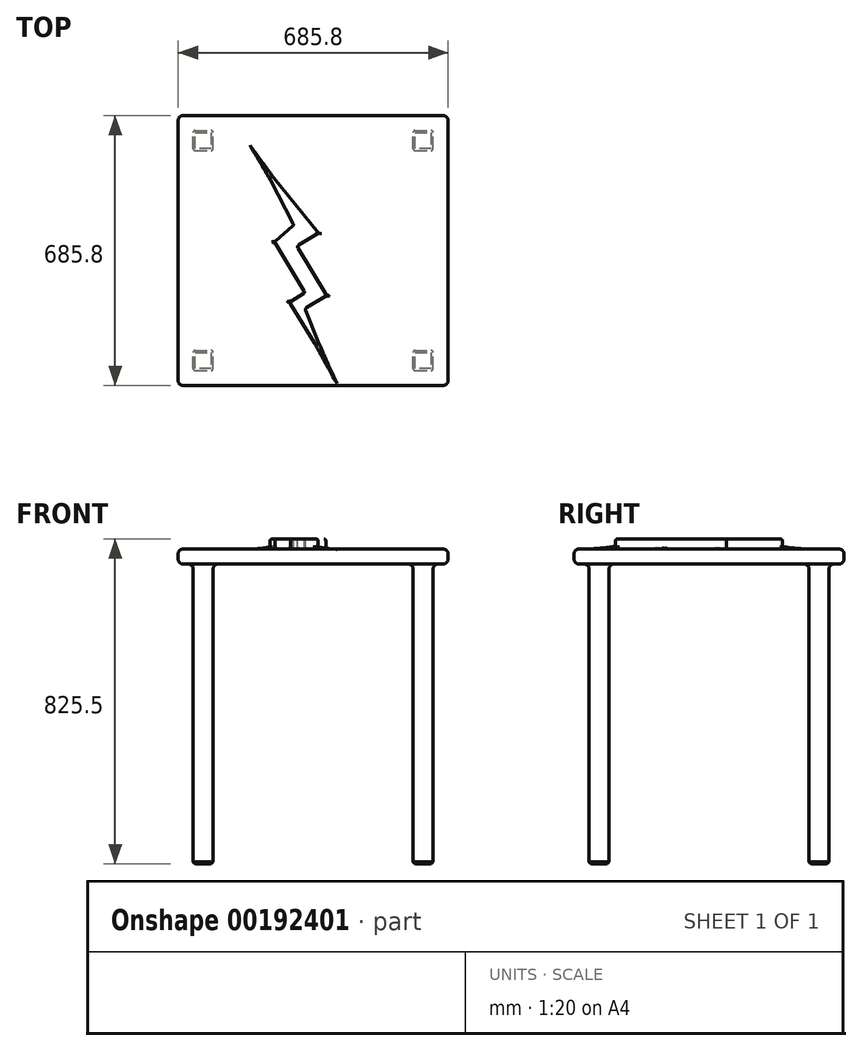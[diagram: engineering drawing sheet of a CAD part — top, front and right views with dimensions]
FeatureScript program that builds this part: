
annotation { "Feature Type Name" : "Feature", "Feature Type Description" : "" }
export const myFeature = defineFeature(function(context is Context, id is Id, definition is map)
    precondition{}
    {
        {
            var Q0;
            Q0=qCreatedBy(makeId("Top.planeOp"),FACE);
            cPlane(context, id + "F0", {"entities" : qUnion([Q0]), "cplaneType" : CPlaneType.OFFSET, "offset" : 457.2 * mm, "width" : 152.4 * mm, "height" : 152.4 * mm});
        }
        {
            var Q0;
            Q0=qCreatedBy(id+"F0.planeOp",FACE);
            var sketch = newSketch(context, id + "F1", { "sketchPlane" : qUnion([Q0])});
            skLineSegment(sketch, "E0.bottom", {"start": v(-322.49, 342.9) * mm, "end": v(363.31, 342.9) * mm});
            skLineSegment(sketch, "E0.top", {"start": v(-322.49, -342.9) * mm, "end": v(363.31, -342.9) * mm});
            skLineSegment(sketch, "E0.left", {"start": v(-322.49, 342.9) * mm, "end": v(-322.49, -342.9) * mm});
            skLineSegment(sketch, "E0.right", {"start": v(363.31, 342.9) * mm, "end": v(363.31, -342.9) * mm});
            skPoint(sketch, "E0.middle", {"position": v(20.41, 0) * mm});
            skSolve(sketch);
        }
        {
            var Q0;
            Q0=makeQuery(id+"F1.imprint","IMPRINT",FACE,{"disambiguationData":[TD([[makeQuery(id+"F1.imprint","IMPRINT",EDGE,{"derivedFrom":sQuery(id+"F1.wireOp",EDGE,"E0.bottom")}),-1.0]])]});
            extrude(context, id + "F2", {"entities" : qUnion([Q0]), "depth" : 38.1 * mm});
        }
        {
            var Q0;
            Q0=makeQuery(id+"F2.opExtrude","CAP_FACE",FACE,{"disambiguationData":[OSD([sQuery(id+"F1.wireOp",EDGE,"E0.bottom"),sQuery(id+"F1.wireOp",EDGE,"E0.top"),sQuery(id+"F1.wireOp",EDGE,"E0.left"),sQuery(id+"F1.wireOp",EDGE,"E0.right")])],"isStart":true});
            var sketch = newSketch(context, id + "F3", { "sketchPlane" : qUnion([Q0])});
            skLineSegment(sketch, "E1.bottom", {"start": v(-284.39, 304.8) * mm, "end": v(-233.59, 304.8) * mm});
            skLineSegment(sketch, "E1.top", {"start": v(-284.39, 254) * mm, "end": v(-233.59, 254) * mm});
            skLineSegment(sketch, "E1.left", {"start": v(-284.39, 304.8) * mm, "end": v(-284.39, 254) * mm});
            skLineSegment(sketch, "E1.right", {"start": v(-233.59, 304.8) * mm, "end": v(-233.59, 254) * mm});
            skPoint(sketch, "E1.middle", {"position": v(-258.99, 279.4) * mm});
            skLineSegment(sketch, "E2.bottom", {"start": v(274.41, 304.8) * mm, "end": v(325.21, 304.8) * mm});
            skLineSegment(sketch, "E2.top", {"start": v(274.41, 254) * mm, "end": v(325.21, 254) * mm});
            skLineSegment(sketch, "E2.left", {"start": v(274.41, 304.8) * mm, "end": v(274.41, 254) * mm});
            skLineSegment(sketch, "E2.right", {"start": v(325.21, 304.8) * mm, "end": v(325.21, 254) * mm});
            skPoint(sketch, "E2.middle", {"position": v(299.81, 279.4) * mm});
            skPoint(sketch, "E3.MirrorP", {"position": v(202.34, 274.07) * mm});
            skLineSegment(sketch, "E4.bottom", {"start": v(274.41, -254) * mm, "end": v(325.21, -254) * mm});
            skLineSegment(sketch, "E4.top", {"start": v(274.41, -304.8) * mm, "end": v(325.21, -304.8) * mm});
            skLineSegment(sketch, "E4.left", {"start": v(274.41, -254) * mm, "end": v(274.41, -304.8) * mm});
            skLineSegment(sketch, "E4.right", {"start": v(325.21, -254) * mm, "end": v(325.21, -304.8) * mm});
            skPoint(sketch, "E4.middle", {"position": v(299.81, -279.4) * mm});
            skLineSegment(sketch, "E5.bottom", {"start": v(-284.39, -254) * mm, "end": v(-233.59, -254) * mm});
            skLineSegment(sketch, "E5.top", {"start": v(-284.39, -304.8) * mm, "end": v(-233.59, -304.8) * mm});
            skLineSegment(sketch, "E5.left", {"start": v(-284.39, -254) * mm, "end": v(-284.39, -304.8) * mm});
            skLineSegment(sketch, "E5.right", {"start": v(-233.59, -254) * mm, "end": v(-233.59, -304.8) * mm});
            skPoint(sketch, "E5.middle", {"position": v(-258.99, -279.4) * mm});
            skSolve(sketch);
        }
        {
            var Q0;
            Q0=makeQuery(id+"F3.imprint","IMPRINT",FACE,{"disambiguationData":[TD([[makeQuery(id+"F3.imprint","IMPRINT",EDGE,{"derivedFrom":sQuery(id+"F3.wireOp",EDGE,"E1.bottom")}),-1.0]])]});
            var Q1;
            Q1=makeQuery(id+"F3.imprint","IMPRINT",FACE,{"disambiguationData":[TD([[makeQuery(id+"F3.imprint","IMPRINT",EDGE,{"derivedFrom":sQuery(id+"F3.wireOp",EDGE,"E5.bottom")}),-1.0]])]});
            var Q2;
            Q2=makeQuery(id+"F3.imprint","IMPRINT",FACE,{"disambiguationData":[TD([[makeQuery(id+"F3.imprint","IMPRINT",EDGE,{"derivedFrom":sQuery(id+"F3.wireOp",EDGE,"E4.bottom")}),-1.0]])]});
            var Q3;
            Q3=makeQuery(id+"F3.imprint","IMPRINT",FACE,{"disambiguationData":[TD([[makeQuery(id+"F3.imprint","IMPRINT",EDGE,{"derivedFrom":sQuery(id+"F3.wireOp",EDGE,"E2.bottom")}),-1.0]])]});
            extrude(context, id + "F4", {"entities" : qUnion([Q0, Q1, Q2, Q3]), "operationType" : NewBodyOperationType.ADD, "depth" : 762 * mm});
        }
        {
            var Q0;
            Q0=makeQuery(id+"F4.opExtrude","SWEPT_EDGE",EDGE,{"disambiguationData":[OSD([sQuery(id+"F3.wireOp",EDGE,"E1.bottom"),sQuery(id+"F3.wireOp",EDGE,"E1.right")])]});
            var Q1;
            Q1=makeQuery(id+"F4.opExtrude","SWEPT_EDGE",EDGE,{"disambiguationData":[OSD([sQuery(id+"F3.wireOp",EDGE,"E1.bottom"),sQuery(id+"F3.wireOp",EDGE,"E1.left")])]});
            var Q2;
            Q2=makeQuery(id+"F4.opExtrude","SWEPT_EDGE",EDGE,{"disambiguationData":[OSD([sQuery(id+"F3.wireOp",EDGE,"E1.top"),sQuery(id+"F3.wireOp",EDGE,"E1.right")])]});
            var Q3;
            Q3=makeQuery(id+"F4.opExtrude","SWEPT_EDGE",EDGE,{"disambiguationData":[OSD([sQuery(id+"F3.wireOp",EDGE,"E1.top"),sQuery(id+"F3.wireOp",EDGE,"E1.left")])]});
            var Q4;
            Q4=makeQuery(id+"F4.opExtrude","SWEPT_EDGE",EDGE,{"disambiguationData":[OSD([sQuery(id+"F3.wireOp",EDGE,"E5.top"),sQuery(id+"F3.wireOp",EDGE,"E5.left")])]});
            var Q5;
            Q5=makeQuery(id+"F4.opExtrude","SWEPT_EDGE",EDGE,{"disambiguationData":[OSD([sQuery(id+"F3.wireOp",EDGE,"E5.top"),sQuery(id+"F3.wireOp",EDGE,"E5.right")])]});
            var Q6;
            Q6=makeQuery(id+"F4.opExtrude","SWEPT_EDGE",EDGE,{"disambiguationData":[OSD([sQuery(id+"F3.wireOp",EDGE,"E5.bottom"),sQuery(id+"F3.wireOp",EDGE,"E5.left")])]});
            var Q7;
            Q7=makeQuery(id+"F4.opExtrude","SWEPT_EDGE",EDGE,{"disambiguationData":[OSD([sQuery(id+"F3.wireOp",EDGE,"E5.bottom"),sQuery(id+"F3.wireOp",EDGE,"E5.right")])]});
            var Q8;
            Q8=makeQuery(id+"F4.opExtrude","SWEPT_EDGE",EDGE,{"disambiguationData":[OSD([sQuery(id+"F3.wireOp",EDGE,"E4.top"),sQuery(id+"F3.wireOp",EDGE,"E4.left")])]});
            var Q9;
            Q9=makeQuery(id+"F4.opExtrude","SWEPT_EDGE",EDGE,{"disambiguationData":[OSD([sQuery(id+"F3.wireOp",EDGE,"E4.top"),sQuery(id+"F3.wireOp",EDGE,"E4.right")])]});
            var Q10;
            Q10=makeQuery(id+"F4.opExtrude","SWEPT_EDGE",EDGE,{"disambiguationData":[OSD([sQuery(id+"F3.wireOp",EDGE,"E4.bottom"),sQuery(id+"F3.wireOp",EDGE,"E4.right")])]});
            var Q11;
            Q11=makeQuery(id+"F4.opExtrude","SWEPT_EDGE",EDGE,{"disambiguationData":[OSD([sQuery(id+"F3.wireOp",EDGE,"E2.top"),sQuery(id+"F3.wireOp",EDGE,"E2.right")])]});
            var Q12;
            Q12=makeQuery(id+"F4.opExtrude","SWEPT_EDGE",EDGE,{"disambiguationData":[OSD([sQuery(id+"F3.wireOp",EDGE,"E2.top"),sQuery(id+"F3.wireOp",EDGE,"E2.left")])]});
            var Q13;
            Q13=makeQuery(id+"F4.opExtrude","SWEPT_EDGE",EDGE,{"disambiguationData":[OSD([sQuery(id+"F3.wireOp",EDGE,"E2.bottom"),sQuery(id+"F3.wireOp",EDGE,"E2.right")])]});
            var Q14;
            Q14=makeQuery(id+"F4.opExtrude","SWEPT_EDGE",EDGE,{"disambiguationData":[OSD([sQuery(id+"F3.wireOp",EDGE,"E2.bottom"),sQuery(id+"F3.wireOp",EDGE,"E2.left")])]});
            var Q15;
            Q15=makeQuery(id+"F4.opExtrude","SWEPT_EDGE",EDGE,{"disambiguationData":[OSD([sQuery(id+"F3.wireOp",EDGE,"E4.bottom"),sQuery(id+"F3.wireOp",EDGE,"E4.left")])]});
            fillet(context, id + "F5", {"entities" : qUnion([Q0, Q1, Q2, Q3, Q4, Q5, Q6, Q7, Q8, Q9, Q10, Q11, Q12, Q13, Q14, Q15]), "radius" : 5.08 * mm, "tangentPropagation" : true, "allowEdgeOverflow" : false});
        }
        {
            var Q0;
            Q0=makeQuery(id+"F4.opExtrude","CAP_FACE",FACE,{"disambiguationData":[OSD([sQuery(id+"F3.wireOp",EDGE,"E2.bottom"),sQuery(id+"F3.wireOp",EDGE,"E2.top"),sQuery(id+"F3.wireOp",EDGE,"E2.left"),sQuery(id+"F3.wireOp",EDGE,"E2.right")])],"isStart":false});
            var Q1;
            Q1=makeQuery(id+"F4.opExtrude","CAP_FACE",FACE,{"disambiguationData":[OSD([sQuery(id+"F3.wireOp",EDGE,"E1.bottom"),sQuery(id+"F3.wireOp",EDGE,"E1.top"),sQuery(id+"F3.wireOp",EDGE,"E1.left"),sQuery(id+"F3.wireOp",EDGE,"E1.right")])],"isStart":false});
            var Q2;
            Q2=makeQuery(id+"F4.opExtrude","CAP_FACE",FACE,{"disambiguationData":[OSD([sQuery(id+"F3.wireOp",EDGE,"E4.bottom"),sQuery(id+"F3.wireOp",EDGE,"E4.top"),sQuery(id+"F3.wireOp",EDGE,"E4.left"),sQuery(id+"F3.wireOp",EDGE,"E4.right")])],"isStart":false});
            chamfer(context, id + "F6", {"entities" : qUnion([Q0, Q1, Q2]), "width" : 5.08 * mm, "tangentPropagation" : true});
        }
        {
            var Q0;
            Q0=makeQuery(id+"F4.opExtrude","CAP_FACE",FACE,{"disambiguationData":[OSD([sQuery(id+"F3.wireOp",EDGE,"E5.bottom"),sQuery(id+"F3.wireOp",EDGE,"E5.top"),sQuery(id+"F3.wireOp",EDGE,"E5.left"),sQuery(id+"F3.wireOp",EDGE,"E5.right")])],"isStart":false});
            chamfer(context, id + "F7", {"entities" : qUnion([Q0]), "width" : 5.08 * mm, "tangentPropagation" : true});
        }
        {
            var Q0;
            Q0=makeQuery(id+"F2.opExtrude","SWEPT_FACE",FACE,{"disambiguationData":[OSD([sQuery(id+"F1.wireOp",EDGE,"E0.top")])]});
            var Q1;
            Q1=makeQuery(id+"F2.opExtrude","SWEPT_FACE",FACE,{"disambiguationData":[OSD([sQuery(id+"F1.wireOp",EDGE,"E0.left")])]});
            var Q2;
            Q2=makeQuery(id+"F2.opExtrude","SWEPT_FACE",FACE,{"disambiguationData":[OSD([sQuery(id+"F1.wireOp",EDGE,"E0.bottom")])]});
            var Q3;
            Q3=makeQuery(id+"F2.opExtrude","SWEPT_FACE",FACE,{"disambiguationData":[OSD([sQuery(id+"F1.wireOp",EDGE,"E0.right")])]});
            var Q4;
            Q4=makeQuery(id+"F2.opExtrude","CAP_FACE",FACE,{"disambiguationData":[OSD([sQuery(id+"F1.wireOp",EDGE,"E0.bottom"),sQuery(id+"F1.wireOp",EDGE,"E0.top"),sQuery(id+"F1.wireOp",EDGE,"E0.left"),sQuery(id+"F1.wireOp",EDGE,"E0.right")])],"isStart":false});
            var Q5;
            Q5=makeQuery(id+"F2.opExtrude","CAP_FACE",FACE,{"disambiguationData":[OSD([sQuery(id+"F1.wireOp",EDGE,"E0.bottom"),sQuery(id+"F1.wireOp",EDGE,"E0.top"),sQuery(id+"F1.wireOp",EDGE,"E0.left"),sQuery(id+"F1.wireOp",EDGE,"E0.right")])],"isStart":true});
            fillet(context, id + "F8", {"entities" : qUnion([Q0, Q1, Q2, Q3, Q4, Q5]), "radius" : 12.7 * mm, "tangentPropagation" : true, "allowEdgeOverflow" : false});
        }
        {
            var Q0;
            Q0=makeQuery(id+"F2.opExtrude","CAP_FACE",FACE,{"disambiguationData":[OSD([sQuery(id+"F1.wireOp",EDGE,"E0.bottom"),sQuery(id+"F1.wireOp",EDGE,"E0.top"),sQuery(id+"F1.wireOp",EDGE,"E0.left"),sQuery(id+"F1.wireOp",EDGE,"E0.right")])],"isStart":false});
            var sketch = newSketch(context, id + "F9", { "sketchPlane" : qUnion([Q0])});
            skLineSegment(sketch, "E6", {"start": v(-112.18, 224.79) * mm, "end": v(-28.45, 64.86) * mm});
            skLineSegment(sketch, "E7", {"start": v(-28.45, 64.86) * mm, "end": v(-77.77, 21.02) * mm});
            skLineSegment(sketch, "E8", {"start": v(-77.77, 21.02) * mm, "end": v(0, -107.1) * mm});
            skLineSegment(sketch, "E9", {"start": v(0, -107.1) * mm, "end": v(-39.5, -131.08) * mm});
            skLineSegment(sketch, "E10", {"start": v(-39.5, -131.08) * mm, "end": v(54.73, -286.32) * mm});
            skLineSegment(sketch, "E11", {"start": v(54.73, -286.32) * mm, "end": v(0, -147.18) * mm});
            skLineSegment(sketch, "E12", {"start": v(0, -147.18) * mm, "end": v(54.73, -113.95) * mm});
            skLineSegment(sketch, "E13", {"start": v(54.73, -113.95) * mm, "end": v(-21.01, 10.82) * mm});
            skLineSegment(sketch, "E14", {"start": v(-21.01, 10.82) * mm, "end": v(33.95, 44.19) * mm});
            skLineSegment(sketch, "E15", {"start": v(33.95, 44.19) * mm, "end": v(-112.18, 224.79) * mm});
            skSolve(sketch);
        }
        {
            var Q0;
            Q0=makeQuery(id+"F9.imprint","IMPRINT",FACE,{"disambiguationData":[TD([[makeQuery(id+"F9.imprint","IMPRINT",EDGE,{"derivedFrom":sQuery(id+"F9.wireOp",EDGE,"E6")}),1.0]])]});
            extrude(context, id + "F10", {"entities" : qUnion([Q0]), "operationType" : NewBodyOperationType.ADD, "depth" : 25.4 * mm});
        }
        {
            var Q0;
            Q0=makeQuery(id+"F2.opExtrude","CAP_FACE",FACE,{"disambiguationData":[OSD([sQuery(id+"F1.wireOp",EDGE,"E0.bottom"),sQuery(id+"F1.wireOp",EDGE,"E0.top"),sQuery(id+"F1.wireOp",EDGE,"E0.left"),sQuery(id+"F1.wireOp",EDGE,"E0.right")])],"isStart":false});
            fillet(context, id + "F11", {"entities" : qUnion([Q0]), "radius" : 5.08 * mm, "tangentPropagation" : true, "allowEdgeOverflow" : false});
        }
        {
            var Q0;
            Q0=makeQuery(id+"F10.opExtrude","CAP_EDGE",EDGE,{"disambiguationData":[OSD([sQuery(id+"F9.wireOp",EDGE,"E7")])],"isStart":false});
            var Q1;
            Q1=makeQuery(id+"F10.opExtrude","CAP_EDGE",EDGE,{"disambiguationData":[OSD([sQuery(id+"F9.wireOp",EDGE,"E8")])],"isStart":false});
            var Q2;
            {var subQ0=sQuery(id+"F9.wireOp",EDGE,"E11");Q2=makeQuery(id+"F11.opFillet","BLEND_EDGE",EDGE,{"blendedFrom":[makeQuery(id+"F10.opExtrude","CAP_EDGE",EDGE,{"disambiguationData":[OSD([subQ0])],"isStart":true}),makeQuery(id+"F10.opExtrude","SWEPT_FACE",FACE,{"disambiguationData":[OSD([subQ0])]})],"blendedInto":[makeQuery(id+"F10.opExtrude","SWEPT_FACE",FACE,{"disambiguationData":[OSD([subQ0])]})]});}
            var Q3;
            {var subQ0=sQuery(id+"F9.wireOp",EDGE,"E10");Q3=makeQuery(id+"F11.opFillet","BLEND_EDGE",EDGE,{"blendedFrom":[makeQuery(id+"F10.opExtrude","CAP_EDGE",EDGE,{"disambiguationData":[OSD([subQ0])],"isStart":true}),makeQuery(id+"F10.opExtrude","SWEPT_FACE",FACE,{"disambiguationData":[OSD([subQ0])]})],"blendedInto":[makeQuery(id+"F10.opExtrude","SWEPT_FACE",FACE,{"disambiguationData":[OSD([subQ0])]})]});}
            var Q4;
            Q4=makeQuery(id+"F10.opExtrude","CAP_EDGE",EDGE,{"disambiguationData":[OSD([sQuery(id+"F9.wireOp",EDGE,"E6")])],"isStart":false});
            var Q5;
            Q5=makeQuery(id+"F10.opExtrude","CAP_EDGE",EDGE,{"disambiguationData":[OSD([sQuery(id+"F9.wireOp",EDGE,"E9")])],"isStart":false});
            var Q6;
            Q6=makeQuery(id+"F10.opExtrude","CAP_EDGE",EDGE,{"disambiguationData":[OSD([sQuery(id+"F9.wireOp",EDGE,"E10")])],"isStart":false});
            var Q7;
            Q7=makeQuery(id+"F10.opExtrude","CAP_EDGE",EDGE,{"disambiguationData":[OSD([sQuery(id+"F9.wireOp",EDGE,"E11")])],"isStart":false});
            var Q8;
            Q8=makeQuery(id+"F10.opExtrude","CAP_EDGE",EDGE,{"disambiguationData":[OSD([sQuery(id+"F9.wireOp",EDGE,"E12")])],"isStart":false});
            var Q9;
            Q9=makeQuery(id+"F10.opExtrude","CAP_EDGE",EDGE,{"disambiguationData":[OSD([sQuery(id+"F9.wireOp",EDGE,"E13")])],"isStart":false});
            var Q10;
            {var subQ0=sQuery(id+"F9.wireOp",EDGE,"E14");Q10=makeQuery(id+"F11.opFillet","BLEND_EDGE",EDGE,{"blendedFrom":[makeQuery(id+"F10.opExtrude","CAP_EDGE",EDGE,{"disambiguationData":[OSD([subQ0])],"isStart":true}),makeQuery(id+"F10.opExtrude","SWEPT_FACE",FACE,{"disambiguationData":[OSD([subQ0])]})],"blendedInto":[makeQuery(id+"F10.opExtrude","SWEPT_FACE",FACE,{"disambiguationData":[OSD([subQ0])]})]});}
            var Q11;
            {var subQ0=sQuery(id+"F9.wireOp",EDGE,"E15");Q11=makeQuery(id+"F11.opFillet","BLEND_EDGE",EDGE,{"blendedFrom":[makeQuery(id+"F10.opExtrude","CAP_EDGE",EDGE,{"disambiguationData":[OSD([subQ0])],"isStart":true}),makeQuery(id+"F10.opExtrude","SWEPT_FACE",FACE,{"disambiguationData":[OSD([subQ0])]})],"blendedInto":[makeQuery(id+"F10.opExtrude","SWEPT_FACE",FACE,{"disambiguationData":[OSD([subQ0])]})]});}
            var Q12;
            {var subQ0=sQuery(id+"F9.wireOp",EDGE,"E13");Q12=makeQuery(id+"F11.opFillet","BLEND_EDGE",EDGE,{"blendedFrom":[makeQuery(id+"F10.opExtrude","CAP_EDGE",EDGE,{"disambiguationData":[OSD([subQ0])],"isStart":true}),makeQuery(id+"F10.opExtrude","SWEPT_FACE",FACE,{"disambiguationData":[OSD([subQ0])]})],"blendedInto":[makeQuery(id+"F10.opExtrude","SWEPT_FACE",FACE,{"disambiguationData":[OSD([subQ0])]})]});}
            var Q13;
            {var subQ0=sQuery(id+"F9.wireOp",EDGE,"E12");Q13=makeQuery(id+"F11.opFillet","BLEND_EDGE",EDGE,{"blendedFrom":[makeQuery(id+"F10.opExtrude","CAP_EDGE",EDGE,{"disambiguationData":[OSD([subQ0])],"isStart":true}),makeQuery(id+"F10.opExtrude","SWEPT_FACE",FACE,{"disambiguationData":[OSD([subQ0])]})],"blendedInto":[makeQuery(id+"F10.opExtrude","SWEPT_FACE",FACE,{"disambiguationData":[OSD([subQ0])]})]});}
            var Q14;
            {var subQ0=sQuery(id+"F9.wireOp",EDGE,"E7");Q14=makeQuery(id+"F11.opFillet","BLEND_EDGE",EDGE,{"blendedFrom":[makeQuery(id+"F10.opExtrude","CAP_EDGE",EDGE,{"disambiguationData":[OSD([subQ0])],"isStart":true}),makeQuery(id+"F10.opExtrude","SWEPT_FACE",FACE,{"disambiguationData":[OSD([subQ0])]})],"blendedInto":[makeQuery(id+"F10.opExtrude","SWEPT_FACE",FACE,{"disambiguationData":[OSD([subQ0])]})]});}
            var Q15;
            {var subQ0=sQuery(id+"F9.wireOp",EDGE,"E9");Q15=makeQuery(id+"F11.opFillet","BLEND_EDGE",EDGE,{"blendedFrom":[makeQuery(id+"F10.opExtrude","CAP_EDGE",EDGE,{"disambiguationData":[OSD([subQ0])],"isStart":true}),makeQuery(id+"F10.opExtrude","SWEPT_FACE",FACE,{"disambiguationData":[OSD([subQ0])]})],"blendedInto":[makeQuery(id+"F10.opExtrude","SWEPT_FACE",FACE,{"disambiguationData":[OSD([subQ0])]})]});}
            var Q16;
            {var subQ0=sQuery(id+"F9.wireOp",EDGE,"E8");Q16=makeQuery(id+"F11.opFillet","BLEND_EDGE",EDGE,{"blendedFrom":[makeQuery(id+"F10.opExtrude","CAP_EDGE",EDGE,{"disambiguationData":[OSD([subQ0])],"isStart":true}),makeQuery(id+"F10.opExtrude","SWEPT_FACE",FACE,{"disambiguationData":[OSD([subQ0])]})],"blendedInto":[makeQuery(id+"F10.opExtrude","SWEPT_FACE",FACE,{"disambiguationData":[OSD([subQ0])]})]});}
            var Q17;
            {var subQ0=sQuery(id+"F9.wireOp",EDGE,"E6");Q17=makeQuery(id+"F11.opFillet","BLEND_EDGE",EDGE,{"blendedFrom":[makeQuery(id+"F10.opExtrude","CAP_EDGE",EDGE,{"disambiguationData":[OSD([subQ0])],"isStart":true}),makeQuery(id+"F10.opExtrude","SWEPT_FACE",FACE,{"disambiguationData":[OSD([subQ0])]})],"blendedInto":[makeQuery(id+"F10.opExtrude","SWEPT_FACE",FACE,{"disambiguationData":[OSD([subQ0])]})]});}
            var Q18;
            Q18=makeQuery(id+"F11.opFillet","BLEND_EDGE",EDGE,{"blendedFrom":[makeQuery(id+"F10.opExtrude","CAP_EDGE",EDGE,{"disambiguationData":[OSD([sQuery(id+"F9.wireOp",EDGE,"E6")])],"isStart":true}),makeQuery(id+"F2.opExtrude","CAP_FACE",FACE,{"disambiguationData":[OSD([sQuery(id+"F1.wireOp",EDGE,"E0.bottom"),sQuery(id+"F1.wireOp",EDGE,"E0.top"),sQuery(id+"F1.wireOp",EDGE,"E0.left"),sQuery(id+"F1.wireOp",EDGE,"E0.right")])],"isStart":false})],"blendedInto":[makeQuery(id+"F2.opExtrude","CAP_FACE",FACE,{"disambiguationData":[OSD([sQuery(id+"F1.wireOp",EDGE,"E0.bottom"),sQuery(id+"F1.wireOp",EDGE,"E0.top"),sQuery(id+"F1.wireOp",EDGE,"E0.left"),sQuery(id+"F1.wireOp",EDGE,"E0.right")])],"isStart":false})]});
            var Q19;
            Q19=makeQuery(id+"F11.opFillet","BLEND_EDGE",EDGE,{"blendedFrom":[makeQuery(id+"F10.opExtrude","CAP_EDGE",EDGE,{"disambiguationData":[OSD([sQuery(id+"F9.wireOp",EDGE,"E6")])],"isStart":true}),makeQuery(id+"F10.opExtrude","CAP_EDGE",EDGE,{"disambiguationData":[OSD([sQuery(id+"F9.wireOp",EDGE,"E15")])],"isStart":true})],"blendedInto":[]});
            var Q20;
            Q20=makeQuery(id+"F11.opFillet","BLEND_EDGE",EDGE,{"blendedFrom":[makeQuery(id+"F10.opExtrude","CAP_EDGE",EDGE,{"disambiguationData":[OSD([sQuery(id+"F9.wireOp",EDGE,"E13")])],"isStart":true}),makeQuery(id+"F2.opExtrude","CAP_FACE",FACE,{"disambiguationData":[OSD([sQuery(id+"F1.wireOp",EDGE,"E0.bottom"),sQuery(id+"F1.wireOp",EDGE,"E0.top"),sQuery(id+"F1.wireOp",EDGE,"E0.left"),sQuery(id+"F1.wireOp",EDGE,"E0.right")])],"isStart":false})],"blendedInto":[makeQuery(id+"F2.opExtrude","CAP_FACE",FACE,{"disambiguationData":[OSD([sQuery(id+"F1.wireOp",EDGE,"E0.bottom"),sQuery(id+"F1.wireOp",EDGE,"E0.top"),sQuery(id+"F1.wireOp",EDGE,"E0.left"),sQuery(id+"F1.wireOp",EDGE,"E0.right")])],"isStart":false})]});
            var Q21;
            Q21=makeQuery(id+"F11.opFillet","BLEND_EDGE",EDGE,{"blendedFrom":[makeQuery(id+"F10.opExtrude","CAP_EDGE",EDGE,{"disambiguationData":[OSD([sQuery(id+"F9.wireOp",EDGE,"E7")])],"isStart":true}),makeQuery(id+"F10.opExtrude","CAP_EDGE",EDGE,{"disambiguationData":[OSD([sQuery(id+"F9.wireOp",EDGE,"E8")])],"isStart":true})],"blendedInto":[]});
            var Q22;
            Q22=makeQuery(id+"F11.opFillet","BLEND_EDGE",EDGE,{"blendedFrom":[makeQuery(id+"F10.opExtrude","CAP_EDGE",EDGE,{"disambiguationData":[OSD([sQuery(id+"F9.wireOp",EDGE,"E7")])],"isStart":true}),makeQuery(id+"F2.opExtrude","CAP_FACE",FACE,{"disambiguationData":[OSD([sQuery(id+"F1.wireOp",EDGE,"E0.bottom"),sQuery(id+"F1.wireOp",EDGE,"E0.top"),sQuery(id+"F1.wireOp",EDGE,"E0.left"),sQuery(id+"F1.wireOp",EDGE,"E0.right")])],"isStart":false})],"blendedInto":[makeQuery(id+"F2.opExtrude","CAP_FACE",FACE,{"disambiguationData":[OSD([sQuery(id+"F1.wireOp",EDGE,"E0.bottom"),sQuery(id+"F1.wireOp",EDGE,"E0.top"),sQuery(id+"F1.wireOp",EDGE,"E0.left"),sQuery(id+"F1.wireOp",EDGE,"E0.right")])],"isStart":false})]});
            var Q23;
            Q23=makeQuery(id+"F11.opFillet","BLEND_EDGE",EDGE,{"blendedFrom":[makeQuery(id+"F10.opExtrude","CAP_EDGE",EDGE,{"disambiguationData":[OSD([sQuery(id+"F9.wireOp",EDGE,"E8")])],"isStart":true}),makeQuery(id+"F2.opExtrude","CAP_FACE",FACE,{"disambiguationData":[OSD([sQuery(id+"F1.wireOp",EDGE,"E0.bottom"),sQuery(id+"F1.wireOp",EDGE,"E0.top"),sQuery(id+"F1.wireOp",EDGE,"E0.left"),sQuery(id+"F1.wireOp",EDGE,"E0.right")])],"isStart":false})],"blendedInto":[makeQuery(id+"F2.opExtrude","CAP_FACE",FACE,{"disambiguationData":[OSD([sQuery(id+"F1.wireOp",EDGE,"E0.bottom"),sQuery(id+"F1.wireOp",EDGE,"E0.top"),sQuery(id+"F1.wireOp",EDGE,"E0.left"),sQuery(id+"F1.wireOp",EDGE,"E0.right")])],"isStart":false})]});
            var Q24;
            Q24=makeQuery(id+"F10.opExtrude","SWEPT_EDGE",EDGE,{"disambiguationData":[OSD([sQuery(id+"F9.wireOp",EDGE,"E6"),sQuery(id+"F9.wireOp",EDGE,"E15")])]});
            var Q25;
            Q25=makeQuery(id+"F11.opFillet","BLEND_EDGE",EDGE,{"blendedFrom":[makeQuery(id+"F10.opExtrude","CAP_EDGE",EDGE,{"disambiguationData":[OSD([sQuery(id+"F9.wireOp",EDGE,"E9")])],"isStart":true}),makeQuery(id+"F10.opExtrude","CAP_EDGE",EDGE,{"disambiguationData":[OSD([sQuery(id+"F9.wireOp",EDGE,"E10")])],"isStart":true})],"blendedInto":[]});
            var Q26;
            Q26=makeQuery(id+"F10.opExtrude","SWEPT_EDGE",EDGE,{"disambiguationData":[OSD([sQuery(id+"F9.wireOp",EDGE,"E6"),sQuery(id+"F9.wireOp",EDGE,"E7")])]});
            var Q27;
            Q27=makeQuery(id+"F11.opFillet","BLEND_EDGE",EDGE,{"blendedFrom":[makeQuery(id+"F10.opExtrude","CAP_EDGE",EDGE,{"disambiguationData":[OSD([sQuery(id+"F9.wireOp",EDGE,"E9")])],"isStart":true}),makeQuery(id+"F2.opExtrude","CAP_FACE",FACE,{"disambiguationData":[OSD([sQuery(id+"F1.wireOp",EDGE,"E0.bottom"),sQuery(id+"F1.wireOp",EDGE,"E0.top"),sQuery(id+"F1.wireOp",EDGE,"E0.left"),sQuery(id+"F1.wireOp",EDGE,"E0.right")])],"isStart":false})],"blendedInto":[makeQuery(id+"F2.opExtrude","CAP_FACE",FACE,{"disambiguationData":[OSD([sQuery(id+"F1.wireOp",EDGE,"E0.bottom"),sQuery(id+"F1.wireOp",EDGE,"E0.top"),sQuery(id+"F1.wireOp",EDGE,"E0.left"),sQuery(id+"F1.wireOp",EDGE,"E0.right")])],"isStart":false})]});
            var Q28;
            Q28=makeQuery(id+"F10.opExtrude","SWEPT_EDGE",EDGE,{"disambiguationData":[OSD([sQuery(id+"F9.wireOp",EDGE,"E7"),sQuery(id+"F9.wireOp",EDGE,"E8")])]});
            var Q29;
            Q29=makeQuery(id+"F10.opExtrude","SWEPT_EDGE",EDGE,{"disambiguationData":[OSD([sQuery(id+"F9.wireOp",EDGE,"E8"),sQuery(id+"F9.wireOp",EDGE,"E9")])]});
            var Q30;
            Q30=makeQuery(id+"F10.opExtrude","SWEPT_EDGE",EDGE,{"disambiguationData":[OSD([sQuery(id+"F9.wireOp",EDGE,"E9"),sQuery(id+"F9.wireOp",EDGE,"E10")])]});
            var Q31;
            Q31=makeQuery(id+"F10.opExtrude","SWEPT_EDGE",EDGE,{"disambiguationData":[OSD([sQuery(id+"F9.wireOp",EDGE,"E10"),sQuery(id+"F9.wireOp",EDGE,"E11")])]});
            var Q32;
            Q32=makeQuery(id+"F11.opFillet","BLEND_EDGE",EDGE,{"blendedFrom":[makeQuery(id+"F10.opExtrude","CAP_EDGE",EDGE,{"disambiguationData":[OSD([sQuery(id+"F9.wireOp",EDGE,"E11")])],"isStart":true}),makeQuery(id+"F10.opExtrude","CAP_EDGE",EDGE,{"disambiguationData":[OSD([sQuery(id+"F9.wireOp",EDGE,"E12")])],"isStart":true})],"blendedInto":[]});
            var Q33;
            Q33=makeQuery(id+"F10.opExtrude","SWEPT_EDGE",EDGE,{"disambiguationData":[OSD([sQuery(id+"F9.wireOp",EDGE,"E11"),sQuery(id+"F9.wireOp",EDGE,"E12")])]});
            var Q34;
            Q34=makeQuery(id+"F10.opExtrude","SWEPT_EDGE",EDGE,{"disambiguationData":[OSD([sQuery(id+"F9.wireOp",EDGE,"E12"),sQuery(id+"F9.wireOp",EDGE,"E13")])]});
            var Q35;
            Q35=makeQuery(id+"F11.opFillet","BLEND_EDGE",EDGE,{"blendedFrom":[makeQuery(id+"F10.opExtrude","CAP_EDGE",EDGE,{"disambiguationData":[OSD([sQuery(id+"F9.wireOp",EDGE,"E12")])],"isStart":true}),makeQuery(id+"F10.opExtrude","CAP_EDGE",EDGE,{"disambiguationData":[OSD([sQuery(id+"F9.wireOp",EDGE,"E13")])],"isStart":true})],"blendedInto":[]});
            var Q36;
            Q36=makeQuery(id+"F10.opExtrude","SWEPT_EDGE",EDGE,{"disambiguationData":[OSD([sQuery(id+"F9.wireOp",EDGE,"E13"),sQuery(id+"F9.wireOp",EDGE,"E14")])]});
            var Q37;
            Q37=makeQuery(id+"F11.opFillet","BLEND_EDGE",EDGE,{"blendedFrom":[makeQuery(id+"F10.opExtrude","CAP_EDGE",EDGE,{"disambiguationData":[OSD([sQuery(id+"F9.wireOp",EDGE,"E12")])],"isStart":true}),makeQuery(id+"F2.opExtrude","CAP_FACE",FACE,{"disambiguationData":[OSD([sQuery(id+"F1.wireOp",EDGE,"E0.bottom"),sQuery(id+"F1.wireOp",EDGE,"E0.top"),sQuery(id+"F1.wireOp",EDGE,"E0.left"),sQuery(id+"F1.wireOp",EDGE,"E0.right")])],"isStart":false})],"blendedInto":[makeQuery(id+"F2.opExtrude","CAP_FACE",FACE,{"disambiguationData":[OSD([sQuery(id+"F1.wireOp",EDGE,"E0.bottom"),sQuery(id+"F1.wireOp",EDGE,"E0.top"),sQuery(id+"F1.wireOp",EDGE,"E0.left"),sQuery(id+"F1.wireOp",EDGE,"E0.right")])],"isStart":false})]});
            var Q38;
            Q38=makeQuery(id+"F11.opFillet","BLEND_EDGE",EDGE,{"blendedFrom":[makeQuery(id+"F10.opExtrude","CAP_EDGE",EDGE,{"disambiguationData":[OSD([sQuery(id+"F9.wireOp",EDGE,"E6")])],"isStart":true}),makeQuery(id+"F10.opExtrude","CAP_EDGE",EDGE,{"disambiguationData":[OSD([sQuery(id+"F9.wireOp",EDGE,"E7")])],"isStart":true})],"blendedInto":[]});
            var Q39;
            Q39=makeQuery(id+"F11.opFillet","BLEND_EDGE",EDGE,{"blendedFrom":[makeQuery(id+"F10.opExtrude","CAP_EDGE",EDGE,{"disambiguationData":[OSD([sQuery(id+"F9.wireOp",EDGE,"E13")])],"isStart":true}),makeQuery(id+"F10.opExtrude","CAP_EDGE",EDGE,{"disambiguationData":[OSD([sQuery(id+"F9.wireOp",EDGE,"E14")])],"isStart":true})],"blendedInto":[]});
            var Q40;
            Q40=makeQuery(id+"F11.opFillet","BLEND_EDGE",EDGE,{"blendedFrom":[makeQuery(id+"F10.opExtrude","CAP_EDGE",EDGE,{"disambiguationData":[OSD([sQuery(id+"F9.wireOp",EDGE,"E8")])],"isStart":true}),makeQuery(id+"F10.opExtrude","CAP_EDGE",EDGE,{"disambiguationData":[OSD([sQuery(id+"F9.wireOp",EDGE,"E9")])],"isStart":true})],"blendedInto":[]});
            fillet(context, id + "F12", {"entities" : qUnion([Q0, Q1, Q2, Q3, Q4, Q5, Q6, Q7, Q8, Q9, Q10, Q11, Q12, Q13, Q14, Q15, Q16, Q17, Q18, Q19, Q20, Q21, Q22, Q23, Q24, Q25, Q26, Q27, Q28, Q29, Q30, Q31, Q32, Q33, Q34, Q35, Q36, Q37, Q38, Q39, Q40]), "radius" : 5.08 * mm, "tangentPropagation" : true, "allowEdgeOverflow" : false});
        }
        {
            var Q0;
            Q0=makeQuery(id+"F10.opExtrude","CAP_FACE",FACE,{"disambiguationData":[OSD([sQuery(id+"F9.wireOp",EDGE,"E6"),sQuery(id+"F9.wireOp",EDGE,"E7"),sQuery(id+"F9.wireOp",EDGE,"E8"),sQuery(id+"F9.wireOp",EDGE,"E9"),sQuery(id+"F9.wireOp",EDGE,"E10"),sQuery(id+"F9.wireOp",EDGE,"E11"),sQuery(id+"F9.wireOp",EDGE,"E12"),sQuery(id+"F9.wireOp",EDGE,"E13"),sQuery(id+"F9.wireOp",EDGE,"E14"),sQuery(id+"F9.wireOp",EDGE,"E15")])],"isStart":false});
            fillet(context, id + "F13", {"entities" : qUnion([Q0]), "radius" : 5.08 * mm, "tangentPropagation" : true, "allowEdgeOverflow" : false});
        }
    });
